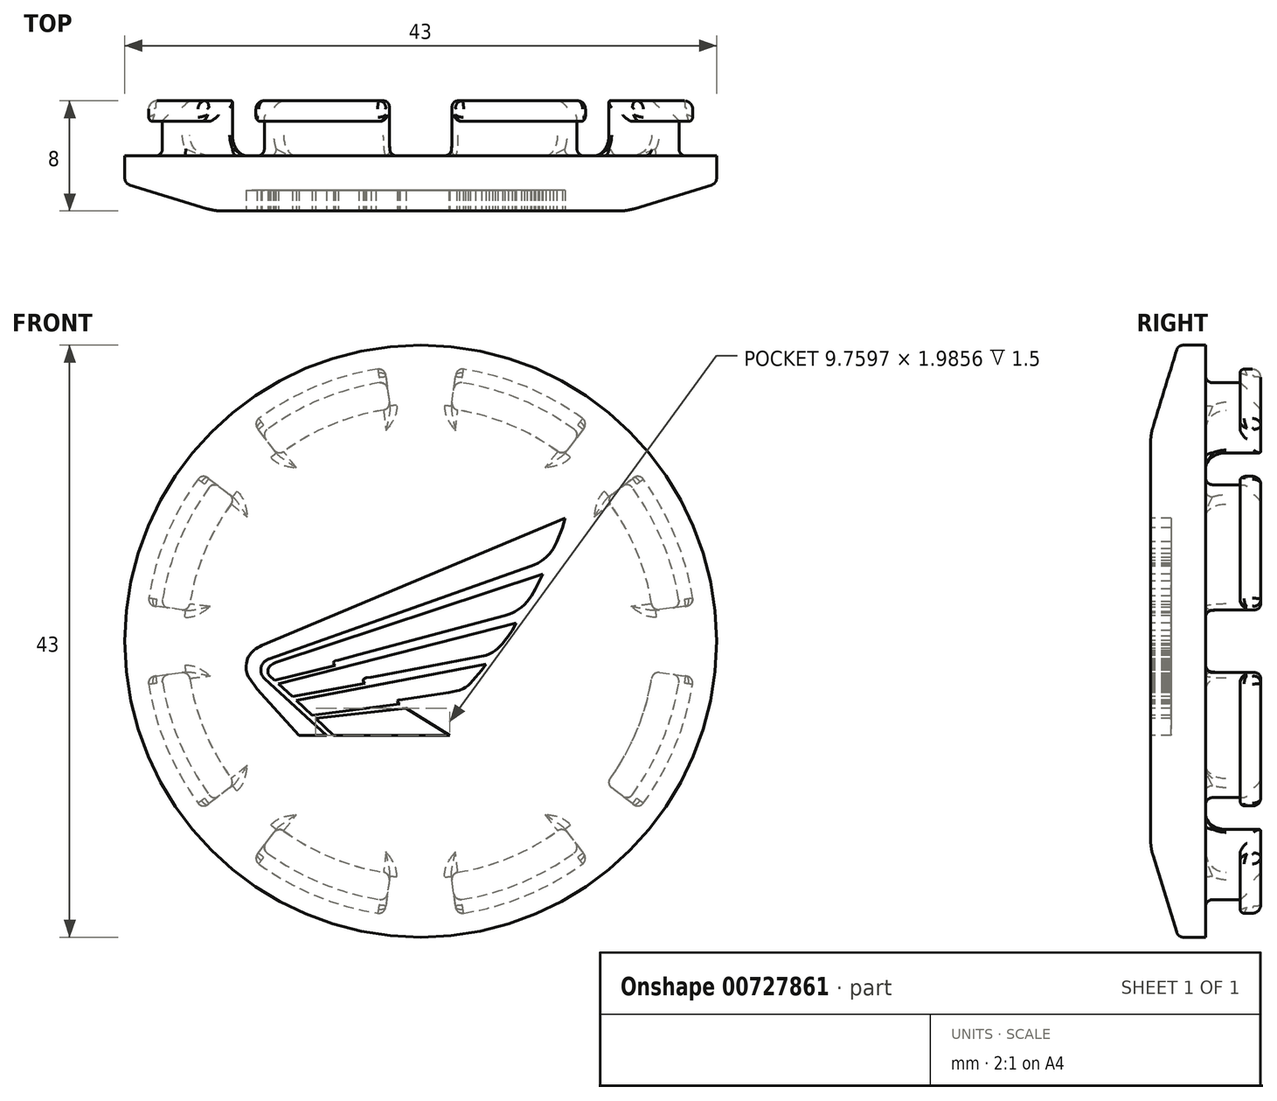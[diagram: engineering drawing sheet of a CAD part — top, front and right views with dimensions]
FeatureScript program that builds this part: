
annotation { "Feature Type Name" : "Feature", "Feature Type Description" : "" }
export const myFeature = defineFeature(function(context is Context, id is Id, definition is map)
    precondition{}
    {
        {
            var Q0;
            Q0=qCreatedBy(makeId("Right.planeOp"),FACE);
            var sketch = newSketch(context, id + "F0", { "sketchPlane" : qUnion([Q0])});
            skLineSegment(sketch, "E0", {"start": v(2.37, 21.5) * mm, "end": v(4, 21.5) * mm});
            skLineSegment(sketch, "E1", {"start": v(4, 21.5) * mm, "end": v(4, 19.5) * mm});
            skLineSegment(sketch, "E2", {"start": v(4, 0) * mm, "end": v(0, 0) * mm});
            skLineSegment(sketch, "E3", {"start": v(1.9, 21.15) * mm, "end": v(0.18, 15.57) * mm});
            skLineSegment(sketch, "E4", {"start": v(0, 14.4) * mm, "end": v(0, 0) * mm});
            skPoint(sketch, "E5.visualSharp", {"position": v(2, 21.5) * mm});
            skArc(sketch, "E5.filletArc", {"start": v(2.37, 21.5) * mm, "mid": v(2.07, 21.4) * mm, "end": v(1.9, 21.15) * mm});
            skPoint(sketch, "E6.visualSharp", {"position": v(0, 15) * mm});
            skArc(sketch, "E6.filletArc", {"start": v(0.18, 15.57) * mm, "mid": v(0.04, 15) * mm, "end": v(0, 14.4) * mm});
            skLineSegment(sketch, "E7", {"start": v(4.5, 19) * mm, "end": v(6.5, 19) * mm});
            skLineSegment(sketch, "E8", {"start": v(6.5, 19) * mm, "end": v(6.5, 19.7) * mm});
            skLineSegment(sketch, "E9", {"start": v(6.8, 20) * mm, "end": v(7.4, 20) * mm});
            skLineSegment(sketch, "E10", {"start": v(8, 19.4) * mm, "end": v(8, 17) * mm});
            skLineSegment(sketch, "E11", {"start": v(8, 17) * mm, "end": v(5.5, 17) * mm});
            skLineSegment(sketch, "E12.trimOffspring", {"start": v(4, 15.5) * mm, "end": v(4, 0) * mm});
            skPoint(sketch, "E13.visualSharp", {"position": v(8, 20) * mm});
            skArc(sketch, "E13.filletArc", {"start": v(8, 19.4) * mm, "mid": v(7.82, 19.82) * mm, "end": v(7.4, 20) * mm});
            skPoint(sketch, "E14.visualSharp", {"position": v(6.5, 20) * mm});
            skArc(sketch, "E14.filletArc", {"start": v(6.8, 20) * mm, "mid": v(6.59, 19.91) * mm, "end": v(6.5, 19.7) * mm});
            skPoint(sketch, "E15.visualSharp", {"position": v(4, 19) * mm});
            skArc(sketch, "E15.filletArc", {"start": v(4, 19.5) * mm, "mid": v(4.15, 19.15) * mm, "end": v(4.5, 19) * mm});
            skPoint(sketch, "E16.visualSharp", {"position": v(4, 17) * mm});
            skArc(sketch, "E16.filletArc", {"start": v(5.5, 17) * mm, "mid": v(4.44, 16.56) * mm, "end": v(4, 15.5) * mm});
            skSolve(sketch);
        }
        {
            var Q0;
            Q0 = qSketchRegion(id + "F0", true);
            var Q1;
            Q1=sQuery(id+"F0.wireOp",EDGE,"E2");
            revolve(context, id + "F1", {"surfaceOperationType" : NewSurfaceOperationType.NEW, "entities" : qUnion([Q0]), "axis" : qUnion([Q1]), "revolveType" : RevolveType.FULL});
        }
        {
            var Q0;
            Q0=makeQuery(id+"F1.opRevolve","SWEPT_FACE",FACE,{"disambiguationData":[OSD([sQuery(id+"F0.wireOp",EDGE,"E10")])]});
            var sketch = newSketch(context, id + "F2", { "sketchPlane" : qUnion([Q0])});
            skLineSegment(sketch, "E17", {"start": v(0, 0) * mm, "end": v(-22.73, -3) * mm});
            skLineSegment(sketch, "E18", {"start": v(-22.73, -3) * mm, "end": v(-22.73, 3) * mm});
            skLineSegment(sketch, "E19", {"start": v(-22.73, 3) * mm, "end": v(0, 0) * mm});
            skLineSegment(sketch, "E20", {"start": v(-22.73, 5.02) * mm, "end": v(-22.73, 3) * mm});
            skLineSegment(sketch, "E21.1.0", {"start": v(0, 0) * mm, "end": v(-13.95, -18.19) * mm});
            skLineSegment(sketch, "E21.1.1", {"start": v(-18.19, -13.95) * mm, "end": v(0, 0) * mm});
            skLineSegment(sketch, "E21.1.2", {"start": v(-13.95, -18.19) * mm, "end": v(-18.19, -13.95) * mm});
            skLineSegment(sketch, "E21.2.0", {"start": v(0, 0) * mm, "end": v(3, -22.73) * mm});
            skLineSegment(sketch, "E21.2.1", {"start": v(-3, -22.73) * mm, "end": v(0, 0) * mm});
            skLineSegment(sketch, "E21.2.2", {"start": v(3, -22.73) * mm, "end": v(-3, -22.73) * mm});
            skLineSegment(sketch, "E21.3.0", {"start": v(0, 0) * mm, "end": v(18.19, -13.95) * mm});
            skLineSegment(sketch, "E21.3.1", {"start": v(13.95, -18.19) * mm, "end": v(0, 0) * mm});
            skLineSegment(sketch, "E21.3.2", {"start": v(18.19, -13.95) * mm, "end": v(13.95, -18.19) * mm});
            skLineSegment(sketch, "E21.4.0", {"start": v(0, 0) * mm, "end": v(22.73, 3) * mm});
            skLineSegment(sketch, "E21.4.1", {"start": v(22.73, -3) * mm, "end": v(0, 0) * mm});
            skLineSegment(sketch, "E21.4.2", {"start": v(22.73, 3) * mm, "end": v(22.73, -3) * mm});
            skLineSegment(sketch, "E21.5.0", {"start": v(0, 0) * mm, "end": v(13.95, 18.19) * mm});
            skLineSegment(sketch, "E21.5.1", {"start": v(18.19, 13.95) * mm, "end": v(0, 0) * mm});
            skLineSegment(sketch, "E21.5.2", {"start": v(13.95, 18.19) * mm, "end": v(18.19, 13.95) * mm});
            skLineSegment(sketch, "E21.6.0", {"start": v(0, 0) * mm, "end": v(-3, 22.73) * mm});
            skLineSegment(sketch, "E21.6.1", {"start": v(3, 22.73) * mm, "end": v(0, 0) * mm});
            skLineSegment(sketch, "E21.6.2", {"start": v(-3, 22.73) * mm, "end": v(3, 22.73) * mm});
            skLineSegment(sketch, "E21.7.0", {"start": v(0, 0) * mm, "end": v(-18.19, 13.95) * mm});
            skLineSegment(sketch, "E21.7.1", {"start": v(-13.95, 18.19) * mm, "end": v(0, 0) * mm});
            skLineSegment(sketch, "E21.7.2", {"start": v(-18.19, 13.95) * mm, "end": v(-13.95, 18.19) * mm});
            skPoint(sketch, "E21.center", {"position": v(0, 0) * mm});
            skSolve(sketch);
        }
        {
            var Q0;
            Q0 = qSketchRegion(id + "F2", true);
            var Q1;
            {var subQ0=sQuery(id+"F2.wireOp",EDGE,"E19");var subQ1=sQuery(id+"F2.wireOp",EDGE,"E17");var subQ2=makeQuery(id+"F2.imprint","INTERSECT",VERTEX,{"derivedFrom":[subQ1,subQ0]});Q1=makeQuery(id+"F2.imprint","IMPRINT",FACE,{"disambiguationData":[TD([[makeQuery(id+"F2.imprint","IMPRINT",EDGE,{"disambiguationData":[TD([[subQ2,-1.0]])],"derivedFrom":subQ1}),1.0]])]});}
            var Q2;
            Q2=makeQuery(id+"F1.opRevolve","SWEPT_FACE",FACE,{"disambiguationData":[OSD([sQuery(id+"F0.wireOp",EDGE,"E12.trimOffspring")])]});
            extrude(context, id + "F3", {"entities" : qUnion([Q0, Q1]), "operationType" : NewBodyOperationType.REMOVE, "endBound" : BoundingType.UP_TO_SURFACE, "oppositeDirection" : true, "depth" : 25 * mm, "endBoundEntityFace" : qUnion([Q2]), "offsetDistance" : 25 * mm});
        }
        {
            var Q0;
            Q0=makeQuery(id+"F3.boolean.opBoolean","COPY",FACE,{"derivedFrom":makeQuery(id+"F3.opExtrude","SWEPT_FACE",FACE,{"disambiguationData":[OSD([sQuery(id+"F2.wireOp",EDGE,"E21.1.1")])]})});
            var Q1;
            Q1=makeQuery(id+"F3.boolean.opBoolean","COPY",FACE,{"derivedFrom":makeQuery(id+"F3.opExtrude","SWEPT_FACE",FACE,{"disambiguationData":[OSD([sQuery(id+"F2.wireOp",EDGE,"E19")])]})});
            var Q2;
            Q2=makeQuery(id+"F3.boolean.opBoolean","COPY",FACE,{"derivedFrom":makeQuery(id+"F3.opExtrude","SWEPT_FACE",FACE,{"disambiguationData":[OSD([sQuery(id+"F2.wireOp",EDGE,"E21.7.1")])]})});
            var Q3;
            Q3=makeQuery(id+"F3.boolean.opBoolean","COPY",FACE,{"derivedFrom":makeQuery(id+"F3.opExtrude","SWEPT_FACE",FACE,{"disambiguationData":[OSD([sQuery(id+"F2.wireOp",EDGE,"E21.6.1")])]})});
            var Q4;
            Q4=makeQuery(id+"F3.boolean.opBoolean","COPY",FACE,{"derivedFrom":makeQuery(id+"F3.opExtrude","SWEPT_FACE",FACE,{"disambiguationData":[OSD([sQuery(id+"F2.wireOp",EDGE,"E21.5.1")])]})});
            var Q5;
            Q5=makeQuery(id+"F3.boolean.opBoolean","COPY",FACE,{"derivedFrom":makeQuery(id+"F3.opExtrude","SWEPT_FACE",FACE,{"disambiguationData":[OSD([sQuery(id+"F2.wireOp",EDGE,"E21.4.1")])]})});
            var Q6;
            Q6=makeQuery(id+"F3.boolean.opBoolean","COPY",FACE,{"derivedFrom":makeQuery(id+"F3.opExtrude","SWEPT_FACE",FACE,{"disambiguationData":[OSD([sQuery(id+"F2.wireOp",EDGE,"E21.3.1")])]})});
            var Q7;
            Q7=makeQuery(id+"F3.boolean.opBoolean","COPY",FACE,{"derivedFrom":makeQuery(id+"F3.opExtrude","SWEPT_FACE",FACE,{"disambiguationData":[OSD([sQuery(id+"F2.wireOp",EDGE,"E21.2.1")])]})});
            var Q8;
            Q8=makeQuery(id+"F3.boolean.opBoolean","COPY",FACE,{"derivedFrom":makeQuery(id+"F3.opExtrude","SWEPT_FACE",FACE,{"disambiguationData":[OSD([sQuery(id+"F2.wireOp",EDGE,"E21.1.0")])]})});
            var Q9;
            Q9=makeQuery(id+"F3.boolean.opBoolean","COPY",FACE,{"derivedFrom":makeQuery(id+"F3.opExtrude","SWEPT_FACE",FACE,{"disambiguationData":[OSD([sQuery(id+"F2.wireOp",EDGE,"E21.2.0")])]})});
            var Q10;
            Q10=makeQuery(id+"F3.boolean.opBoolean","COPY",FACE,{"derivedFrom":makeQuery(id+"F3.opExtrude","SWEPT_FACE",FACE,{"disambiguationData":[OSD([sQuery(id+"F2.wireOp",EDGE,"E21.3.0")])]})});
            var Q11;
            Q11=makeQuery(id+"F3.boolean.opBoolean","COPY",FACE,{"derivedFrom":makeQuery(id+"F3.opExtrude","SWEPT_FACE",FACE,{"disambiguationData":[OSD([sQuery(id+"F2.wireOp",EDGE,"E21.4.0")])]})});
            var Q12;
            Q12=makeQuery(id+"F3.boolean.opBoolean","COPY",FACE,{"derivedFrom":makeQuery(id+"F3.opExtrude","SWEPT_FACE",FACE,{"disambiguationData":[OSD([sQuery(id+"F2.wireOp",EDGE,"E21.5.0")])]})});
            var Q13;
            Q13=makeQuery(id+"F3.boolean.opBoolean","COPY",FACE,{"derivedFrom":makeQuery(id+"F3.opExtrude","SWEPT_FACE",FACE,{"disambiguationData":[OSD([sQuery(id+"F2.wireOp",EDGE,"E21.6.0")])]})});
            var Q14;
            Q14=makeQuery(id+"F3.boolean.opBoolean","COPY",FACE,{"derivedFrom":makeQuery(id+"F3.opExtrude","SWEPT_FACE",FACE,{"disambiguationData":[OSD([sQuery(id+"F2.wireOp",EDGE,"E21.7.0")])]})});
            var Q15;
            Q15=makeQuery(id+"F3.boolean.opBoolean","COPY",FACE,{"derivedFrom":makeQuery(id+"F3.opExtrude","SWEPT_FACE",FACE,{"disambiguationData":[OSD([sQuery(id+"F2.wireOp",EDGE,"E17")])]})});
            fillet(context, id + "F4", {"entities" : qUnion([Q0, Q1, Q2, Q3, Q4, Q5, Q6, Q7, Q8, Q9, Q10, Q11, Q12, Q13, Q14, Q15]), "radius" : 0.5 * mm, "tangentPropagation" : true, "allowEdgeOverflow" : false});
        }
        {
            var Q0;
            Q0=makeQuery(id+"F1.opRevolve","SWEPT_FACE",FACE,{"disambiguationData":[OSD([sQuery(id+"F0.wireOp",EDGE,"E4")])]});
            var sketch = newSketch(context, id + "F5", { "sketchPlane" : qUnion([Q0])});
            skLineSegment(sketch, "E22", {"start": v(10.48, 8.95) * mm, "end": v(-11.54, -0.3) * mm});
            skLineSegment(sketch, "E23", {"start": v(-8.85, -6.85) * mm, "end": v(-11.88, -3.5) * mm});
            skFitSpline(sketch, "E24", {"points": [v(-11.54, -0.3) * mm, v(-12.02, -0.58) * mm, v(-12.27, -0.84) * mm, v(-12.51, -1.13) * mm, v(-12.66, -1.67) * mm, v(-12.66, -2.14) * mm, v(-12.6, -2.42) * mm, v(-11.88, -3.5) * mm], "startDerivative": vector(-3.45, -2.15) * mm, "endDerivative": vector(5.4, -7.72) * mm});
            skLineSegment(sketch, "E25", {"start": v(-8.85, -6.85) * mm, "end": v(-6.84, -6.85) * mm});
            skLineSegment(sketch, "E26", {"start": v(-6.84, -6.85) * mm, "end": v(-11.34, -2.73) * mm});
            skLineSegment(sketch, "E27", {"start": v(-11, -1.28) * mm, "end": v(7.97, 5.45) * mm});
            skArc(sketch, "E28", {"start": v(-11, -1.28) * mm, "mid": v(-11.6, -1.9) * mm, "end": v(-11.34, -2.73) * mm});
            skLineSegment(sketch, "E29", {"start": v(10.48, 8.95) * mm, "end": v(10.3, 8.23) * mm});
            skLineSegment(sketch, "E30", {"start": v(10.3, 8.23) * mm, "end": v(9.9, 7.21) * mm});
            skLineSegment(sketch, "E31", {"start": v(9.9, 7.21) * mm, "end": v(9.65, 6.73) * mm});
            skLineSegment(sketch, "E32", {"start": v(9.65, 6.73) * mm, "end": v(9.39, 6.37) * mm});
            skLineSegment(sketch, "E33", {"start": v(9.39, 6.37) * mm, "end": v(9.08, 6.08) * mm});
            skLineSegment(sketch, "E34", {"start": v(9.08, 6.08) * mm, "end": v(8.8, 5.85) * mm});
            skLineSegment(sketch, "E35", {"start": v(8.8, 5.85) * mm, "end": v(8.52, 5.66) * mm});
            skLineSegment(sketch, "E36", {"start": v(8.52, 5.66) * mm, "end": v(8.24, 5.54) * mm});
            skLineSegment(sketch, "E37", {"start": v(8.24, 5.54) * mm, "end": v(7.97, 5.45) * mm});
            skLineSegment(sketch, "E38", {"start": v(8.86, 4.88) * mm, "end": v(-10.52, -1.54) * mm});
            skLineSegment(sketch, "E39", {"start": v(-10.52, -1.54) * mm, "end": v(-10.73, -1.63) * mm});
            skLineSegment(sketch, "E40", {"start": v(-10.73, -1.63) * mm, "end": v(-10.9, -1.77) * mm});
            skLineSegment(sketch, "E41", {"start": v(-10.9, -1.77) * mm, "end": v(-11, -1.86) * mm});
            skLineSegment(sketch, "E42", {"start": v(-11, -1.86) * mm, "end": v(-11.04, -1.93) * mm});
            skLineSegment(sketch, "E43", {"start": v(-11.04, -1.93) * mm, "end": v(-11.08, -2.06) * mm});
            skLineSegment(sketch, "E44", {"start": v(-11.08, -2.06) * mm, "end": v(-11.08, -2.22) * mm});
            skLineSegment(sketch, "E45", {"start": v(-11.08, -2.22) * mm, "end": v(-11.08, -2.33) * mm});
            skLineSegment(sketch, "E46", {"start": v(-11.08, -2.33) * mm, "end": v(-11.05, -2.41) * mm});
            skLineSegment(sketch, "E47", {"start": v(-11.05, -2.41) * mm, "end": v(-11.01, -2.5) * mm});
            skLineSegment(sketch, "E48", {"start": v(-11.01, -2.5) * mm, "end": v(-10.63, -2.86) * mm});
            skLineSegment(sketch, "E49", {"start": v(-10.63, -2.86) * mm, "end": v(-6.2, -1.78) * mm});
            skLineSegment(sketch, "E50", {"start": v(-6.2, -1.78) * mm, "end": v(-6.3, -1.69) * mm});
            skLineSegment(sketch, "E51", {"start": v(-6.3, -1.69) * mm, "end": v(-6.32, -1.58) * mm});
            skLineSegment(sketch, "E52", {"start": v(-6.32, -1.58) * mm, "end": v(-6.3, -1.48) * mm});
            skLineSegment(sketch, "E53", {"start": v(-6.3, -1.48) * mm, "end": v(-6.2, -1.42) * mm});
            skLineSegment(sketch, "E54", {"start": v(-6.2, -1.42) * mm, "end": v(-5.98, -1.37) * mm});
            skLineSegment(sketch, "E55", {"start": v(-5.98, -1.37) * mm, "end": v(-4.5, -0.96) * mm});
            skLineSegment(sketch, "E56", {"start": v(-4.5, -0.96) * mm, "end": v(6.13, 1.84) * mm});
            skLineSegment(sketch, "E57", {"start": v(8.86, 4.88) * mm, "end": v(8.63, 4.35) * mm});
            skLineSegment(sketch, "E58", {"start": v(8.63, 4.35) * mm, "end": v(8.35, 3.79) * mm});
            skLineSegment(sketch, "E59", {"start": v(8.35, 3.79) * mm, "end": v(8.04, 3.28) * mm});
            skLineSegment(sketch, "E60", {"start": v(8.04, 3.28) * mm, "end": v(7.74, 2.89) * mm});
            skLineSegment(sketch, "E61", {"start": v(7.74, 2.89) * mm, "end": v(7.55, 2.66) * mm});
            skLineSegment(sketch, "E62", {"start": v(7.55, 2.66) * mm, "end": v(7.33, 2.47) * mm});
            skLineSegment(sketch, "E63", {"start": v(7.33, 2.47) * mm, "end": v(7.03, 2.26) * mm});
            skLineSegment(sketch, "E64", {"start": v(7.03, 2.26) * mm, "end": v(6.86, 2.14) * mm});
            skLineSegment(sketch, "E65", {"start": v(6.86, 2.14) * mm, "end": v(6.65, 2.03) * mm});
            skLineSegment(sketch, "E66", {"start": v(6.65, 2.03) * mm, "end": v(6.41, 1.95) * mm});
            skLineSegment(sketch, "E67", {"start": v(6.41, 1.95) * mm, "end": v(6.13, 1.84) * mm});
            skLineSegment(sketch, "E68", {"start": v(6.94, 1.33) * mm, "end": v(-10.35, -3.1) * mm});
            skLineSegment(sketch, "E69", {"start": v(-10.35, -3.1) * mm, "end": v(-9.33, -4.03) * mm});
            skLineSegment(sketch, "E70", {"start": v(-9.33, -4.03) * mm, "end": v(-4.04, -3.07) * mm});
            skLineSegment(sketch, "E71", {"start": v(-4.04, -3.07) * mm, "end": v(-4.15, -2.97) * mm});
            skLineSegment(sketch, "E72", {"start": v(-4.15, -2.97) * mm, "end": v(-4.18, -2.88) * mm});
            skLineSegment(sketch, "E73", {"start": v(-4.18, -2.88) * mm, "end": v(-4.18, -2.78) * mm});
            skLineSegment(sketch, "E74", {"start": v(-4.18, -2.78) * mm, "end": v(-4.09, -2.72) * mm});
            skLineSegment(sketch, "E75", {"start": v(-4.09, -2.72) * mm, "end": v(-3.95, -2.67) * mm});
            skLineSegment(sketch, "E76", {"start": v(-3.95, -2.67) * mm, "end": v(-3.6, -2.61) * mm});
            skLineSegment(sketch, "E77", {"start": v(-3.6, -2.61) * mm, "end": v(-3.24, -2.55) * mm});
            skLineSegment(sketch, "E78", {"start": v(-3.24, -2.55) * mm, "end": v(4.74, -1.02) * mm});
            skLineSegment(sketch, "E79", {"start": v(6.94, 1.33) * mm, "end": v(6.66, 0.78) * mm});
            skLineSegment(sketch, "E80", {"start": v(6.66, 0.78) * mm, "end": v(6.36, 0.35) * mm});
            skLineSegment(sketch, "E81", {"start": v(6.36, 0.35) * mm, "end": v(6.12, 0.05) * mm});
            skLineSegment(sketch, "E82", {"start": v(6.12, 0.05) * mm, "end": v(5.94, -0.17) * mm});
            skLineSegment(sketch, "E83", {"start": v(5.94, -0.17) * mm, "end": v(5.62, -0.53) * mm});
            skLineSegment(sketch, "E84", {"start": v(5.62, -0.53) * mm, "end": v(5.41, -0.7) * mm});
            skLineSegment(sketch, "E85", {"start": v(5.41, -0.7) * mm, "end": v(5.22, -0.81) * mm});
            skLineSegment(sketch, "E86", {"start": v(5.22, -0.81) * mm, "end": v(4.96, -0.95) * mm});
            skLineSegment(sketch, "E87", {"start": v(4.96, -0.95) * mm, "end": v(4.74, -1.02) * mm});
            skLineSegment(sketch, "E88", {"start": v(-9.04, -4.31) * mm, "end": v(4.74, -1.68) * mm});
            skLineSegment(sketch, "E89", {"start": v(4.74, -1.68) * mm, "end": v(4.42, -2.13) * mm});
            skLineSegment(sketch, "E90", {"start": v(4.42, -2.13) * mm, "end": v(4, -2.63) * mm});
            skLineSegment(sketch, "E91", {"start": v(4, -2.63) * mm, "end": v(3.6, -3.06) * mm});
            skLineSegment(sketch, "E92", {"start": v(3.6, -3.06) * mm, "end": v(3.44, -3.22) * mm});
            skLineSegment(sketch, "E93", {"start": v(3.44, -3.22) * mm, "end": v(3.26, -3.35) * mm});
            skLineSegment(sketch, "E94", {"start": v(3.26, -3.35) * mm, "end": v(3.09, -3.44) * mm});
            skLineSegment(sketch, "E95", {"start": v(3.09, -3.44) * mm, "end": v(2.82, -3.57) * mm});
            skLineSegment(sketch, "E96", {"start": v(2.82, -3.57) * mm, "end": v(2.61, -3.62) * mm});
            skLineSegment(sketch, "E97", {"start": v(2.61, -3.62) * mm, "end": v(2.05, -3.73) * mm});
            skLineSegment(sketch, "E98", {"start": v(2.05, -3.73) * mm, "end": v(-1.44, -4.25) * mm});
            skLineSegment(sketch, "E99", {"start": v(-1.44, -4.25) * mm, "end": v(-1.53, -4.26) * mm});
            skLineSegment(sketch, "E100", {"start": v(-1.53, -4.26) * mm, "end": v(-1.62, -4.28) * mm});
            skLineSegment(sketch, "E101", {"start": v(-1.62, -4.28) * mm, "end": v(-1.69, -4.33) * mm});
            skLineSegment(sketch, "E102", {"start": v(-1.69, -4.33) * mm, "end": v(-1.67, -4.4) * mm});
            skLineSegment(sketch, "E103", {"start": v(-1.67, -4.4) * mm, "end": v(-1.64, -4.48) * mm});
            skLineSegment(sketch, "E104", {"start": v(-1.64, -4.48) * mm, "end": v(-1.57, -4.52) * mm});
            skLineSegment(sketch, "E105", {"start": v(-1.57, -4.52) * mm, "end": v(-1.53, -4.55) * mm});
            skLineSegment(sketch, "E106", {"start": v(-1.53, -4.55) * mm, "end": v(-1.5, -4.55) * mm});
            skLineSegment(sketch, "E107", {"start": v(-1.5, -4.55) * mm, "end": v(-7.9, -5.4) * mm});
            skLineSegment(sketch, "E108", {"start": v(-7.9, -5.4) * mm, "end": v(-9.04, -4.31) * mm});
            skLineSegment(sketch, "E109", {"start": v(-7.64, -5.6) * mm, "end": v(-6.33, -6.85) * mm});
            skLineSegment(sketch, "E110", {"start": v(-6.33, -6.85) * mm, "end": v(2.12, -6.85) * mm});
            skLineSegment(sketch, "E111", {"start": v(2.12, -6.85) * mm, "end": v(-1.05, -4.86) * mm});
            skLineSegment(sketch, "E112", {"start": v(-1.05, -4.86) * mm, "end": v(-7.64, -5.6) * mm});
            skSolve(sketch);
        }
        {
            var Q0;
            Q0 = qSketchRegion(id + "F5", true);
            extrude(context, id + "F6", {"entities" : qUnion([Q0]), "operationType" : NewBodyOperationType.REMOVE, "oppositeDirection" : true, "depth" : 1.5 * mm, "offsetDistance" : 25 * mm});
        }
    });
